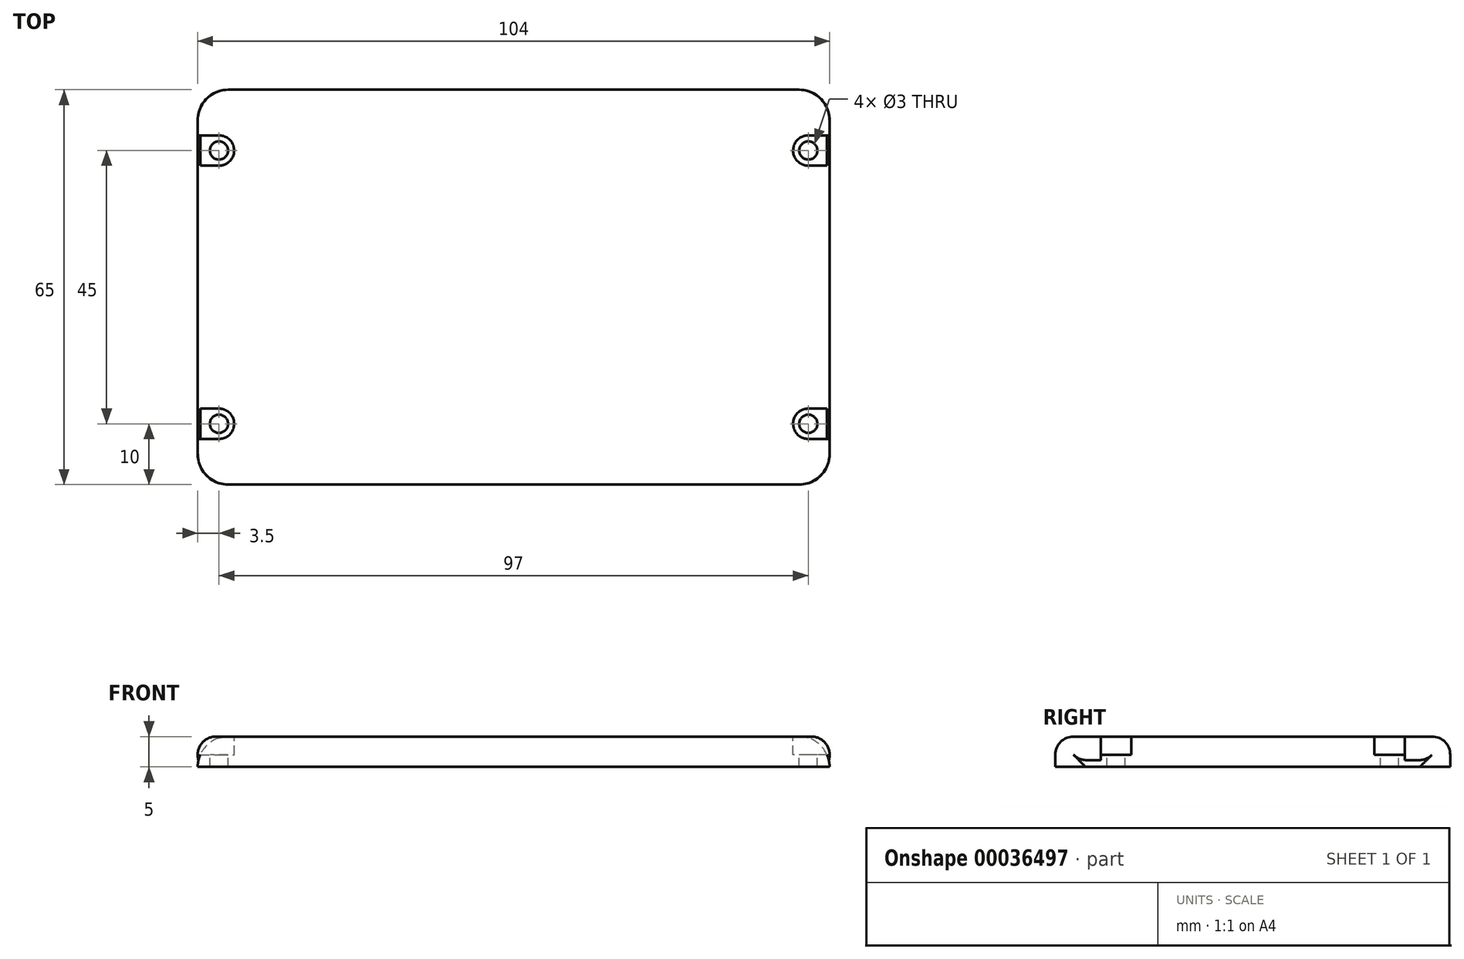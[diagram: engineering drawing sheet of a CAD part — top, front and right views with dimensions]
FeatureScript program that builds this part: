
annotation { "Feature Type Name" : "Feature", "Feature Type Description" : "" }
export const myFeature = defineFeature(function(context is Context, id is Id, definition is map)
    precondition{}
    {
        {
            var Q0;
            Q0=qCreatedBy(makeId("Top.planeOp"),FACE);
            var sketch = newSketch(context, id + "F0", { "sketchPlane" : qUnion([Q0])});
            skLineSegment(sketch, "E0.bottom", {"start": v(5, 0) * mm, "end": v(99, 0) * mm});
            skLineSegment(sketch, "E0.top", {"start": v(5, 65) * mm, "end": v(99, 65) * mm});
            skLineSegment(sketch, "E0.left", {"start": v(0, 5) * mm, "end": v(0, 60) * mm});
            skLineSegment(sketch, "E0.right", {"start": v(104, 5) * mm, "end": v(104, 60) * mm});
            skPoint(sketch, "E1.visualSharp", {"position": v(0, 0) * mm});
            skArc(sketch, "E1.filletArc", {"start": v(0, 5) * mm, "mid": v(1.46, 1.46) * mm, "end": v(5, 0) * mm});
            skPoint(sketch, "E2.visualSharp", {"position": v(0, 65) * mm});
            skArc(sketch, "E2.filletArc", {"start": v(5, 65) * mm, "mid": v(1.46, 63.54) * mm, "end": v(0, 60) * mm});
            skPoint(sketch, "E3.visualSharp", {"position": v(104, 65) * mm});
            skArc(sketch, "E3.filletArc", {"start": v(104, 60) * mm, "mid": v(102.54, 63.54) * mm, "end": v(99, 65) * mm});
            skPoint(sketch, "E4.visualSharp", {"position": v(104, 0) * mm});
            skArc(sketch, "E4.filletArc", {"start": v(99, 0) * mm, "mid": v(102.54, 1.46) * mm, "end": v(104, 5) * mm});
            skSolve(sketch);
        }
        {
            var Q0;
            Q0=makeQuery(id+"F0.imprint","IMPRINT",FACE,{"disambiguationData":[TD([[makeQuery(id+"F0.imprint","IMPRINT",EDGE,{"derivedFrom":sQuery(id+"F0.wireOp",EDGE,"E0.bottom")}),1.0]])]});
            extrude(context, id + "F1", {"entities" : qUnion([Q0]), "depth" : 5 * mm});
        }
        {
            var Q0;
            Q0=makeQuery(id+"F1.opExtrude","CAP_FACE",FACE,{"disambiguationData":[OSD([sQuery(id+"F0.wireOp",EDGE,"E0.bottom"),sQuery(id+"F0.wireOp",EDGE,"E0.top"),sQuery(id+"F0.wireOp",EDGE,"E0.left"),sQuery(id+"F0.wireOp",EDGE,"E0.right"),sQuery(id+"F0.wireOp",EDGE,"E1.filletArc"),sQuery(id+"F0.wireOp",EDGE,"E2.filletArc"),sQuery(id+"F0.wireOp",EDGE,"E3.filletArc"),sQuery(id+"F0.wireOp",EDGE,"E4.filletArc")])],"isStart":false});
            var sketch = newSketch(context, id + "F2", { "sketchPlane" : qUnion([Q0])});
            skCircle(sketch, "E5", {"center": v(3.5, 10) * mm, "radius": 1.5 * mm});
            skCircle(sketch, "E6", {"center": v(100.5, 55) * mm, "radius": 1.5 * mm});
            skLineSegment(sketch, "E7", {"start": v(0, 32.5) * mm, "end": v(104, 32.5) * mm});
            skCircle(sketch, "E8.MirrorC", {"center": v(100.5, 10) * mm, "radius": 1.5 * mm});
            skCircle(sketch, "E9.MirrorC", {"center": v(3.5, 55) * mm, "radius": 1.5 * mm});
            skSolve(sketch);
        }
        {
            var Q0;
            Q0 = qSketchRegion(id + "F2", true);
            extrude(context, id + "F3", {"entities" : qUnion([Q0]), "operationType" : NewBodyOperationType.REMOVE, "oppositeDirection" : true, "depth" : 5 * mm});
        }
        {
            var Q0;
            Q0=makeQuery(id+"F1.opExtrude","CAP_FACE",FACE,{"disambiguationData":[OSD([sQuery(id+"F0.wireOp",EDGE,"E0.bottom"),sQuery(id+"F0.wireOp",EDGE,"E0.top"),sQuery(id+"F0.wireOp",EDGE,"E0.left"),sQuery(id+"F0.wireOp",EDGE,"E0.right"),sQuery(id+"F0.wireOp",EDGE,"E1.filletArc"),sQuery(id+"F0.wireOp",EDGE,"E2.filletArc"),sQuery(id+"F0.wireOp",EDGE,"E3.filletArc"),sQuery(id+"F0.wireOp",EDGE,"E4.filletArc")])],"isStart":false});
            var sketch = newSketch(context, id + "F4", { "sketchPlane" : qUnion([Q0])});
            skLineSegment(sketch, "E10.bottom", {"start": v(0, 12.5) * mm, "end": v(3.5, 12.5) * mm});
            skLineSegment(sketch, "E10.top", {"start": v(0, 7.5) * mm, "end": v(3.5, 7.5) * mm});
            skLineSegment(sketch, "E10.left", {"start": v(0, 12.5) * mm, "end": v(0, 7.5) * mm});
            skLineSegment(sketch, "E10.right", {"start": v(6, 10) * mm, "end": v(6, 10) * mm});
            skPoint(sketch, "E11.visualSharp", {"position": v(6, 12.5) * mm});
            skArc(sketch, "E11.filletArc", {"start": v(6, 10) * mm, "mid": v(5.27, 11.77) * mm, "end": v(3.5, 12.5) * mm});
            skPoint(sketch, "E12.visualSharp", {"position": v(6, 7.5) * mm});
            skArc(sketch, "E12.filletArc", {"start": v(3.5, 7.5) * mm, "mid": v(5.27, 8.23) * mm, "end": v(6, 10) * mm});
            skLineSegment(sketch, "E13.bottom", {"start": v(104, 52.5) * mm, "end": v(100.5, 52.5) * mm});
            skLineSegment(sketch, "E13.top", {"start": v(104, 57.5) * mm, "end": v(100.5, 57.5) * mm});
            skLineSegment(sketch, "E13.left", {"start": v(104, 52.5) * mm, "end": v(104, 57.5) * mm});
            skLineSegment(sketch, "E13.right", {"start": v(98, 55) * mm, "end": v(98, 55) * mm});
            skPoint(sketch, "E14.visualSharp", {"position": v(98, 52.5) * mm});
            skArc(sketch, "E14.filletArc", {"start": v(98, 55) * mm, "mid": v(98.73, 53.23) * mm, "end": v(100.5, 52.5) * mm});
            skPoint(sketch, "E15.visualSharp", {"position": v(98, 57.5) * mm});
            skArc(sketch, "E15.filletArc", {"start": v(100.5, 57.5) * mm, "mid": v(98.73, 56.77) * mm, "end": v(98, 55) * mm});
            skLineSegment(sketch, "E16", {"start": v(0, 32.5) * mm, "end": v(104, 32.5) * mm});
            skLineSegment(sketch, "E17.MirrorCS", {"start": v(0, 52.5) * mm, "end": v(0, 57.5) * mm});
            skLineSegment(sketch, "E18.MirrorCS", {"start": v(0, 52.5) * mm, "end": v(3.5, 52.5) * mm});
            skArc(sketch, "E19.MirrorCS", {"start": v(6, 55) * mm, "mid": v(5.27, 53.23) * mm, "end": v(3.5, 52.5) * mm});
            skArc(sketch, "E20.MirrorCS", {"start": v(3.5, 57.5) * mm, "mid": v(5.27, 56.77) * mm, "end": v(6, 55) * mm});
            skLineSegment(sketch, "E21.MirrorCS", {"start": v(0, 57.5) * mm, "end": v(3.5, 57.5) * mm});
            skLineSegment(sketch, "E22.MirrorCS", {"start": v(104, 12.5) * mm, "end": v(100.5, 12.5) * mm});
            skArc(sketch, "E23.MirrorCS", {"start": v(98, 10) * mm, "mid": v(98.73, 11.77) * mm, "end": v(100.5, 12.5) * mm});
            skArc(sketch, "E24.MirrorCS", {"start": v(100.5, 7.5) * mm, "mid": v(98.73, 8.23) * mm, "end": v(98, 10) * mm});
            skLineSegment(sketch, "E25.MirrorCS", {"start": v(104, 7.5) * mm, "end": v(100.5, 7.5) * mm});
            skLineSegment(sketch, "E26.MirrorCS", {"start": v(104, 12.5) * mm, "end": v(104, 7.5) * mm});
            skSolve(sketch);
        }
        {
            var Q0;
            Q0 = qSketchRegion(id + "F4", true);
            extrude(context, id + "F5", {"entities" : qUnion([Q0]), "operationType" : NewBodyOperationType.REMOVE, "oppositeDirection" : true, "depth" : 3 * mm});
        }
        {
            var Q0;
            {var subQ0=sQuery(id+"F0.wireOp",EDGE,"E0.right");var subQ1=sQuery(id+"F0.wireOp",EDGE,"E4.filletArc");Q0=makeQuery(id+"F5.boolean.opBoolean","SPLIT",EDGE,{"disambiguationData":[TD([makeQuery(id+"F1.opExtrude","SWEPT_FACE",FACE,{"disambiguationData":[OSD([subQ1])]})])],"derivedFrom":makeQuery(id+"F1.opExtrude","CAP_EDGE",EDGE,{"disambiguationData":[OSD([subQ0])],"isStart":false})});}
            fillet(context, id + "F6", {"entities" : qUnion([Q0]), "radius" : 3 * mm, "tangentPropagation" : true, "allowEdgeOverflow" : false});
        }
        {
            var Q0;
            Q0=makeQuery(id+"F1.opExtrude","CAP_EDGE",EDGE,{"disambiguationData":[OSD([sQuery(id+"F0.wireOp",EDGE,"E0.top")])],"isStart":false});
            fillet(context, id + "F7", {"entities" : qUnion([Q0]), "radius" : 3 * mm, "tangentPropagation" : true, "allowEdgeOverflow" : false});
        }
        {
            var Q0;
            {var subQ0=sQuery(id+"F0.wireOp",EDGE,"E0.left");Q0=makeQuery(id+"F5.boolean.opBoolean","SPLIT",EDGE,{"disambiguationData":[TD([makeQuery(id+"F5.opExtrude","SWEPT_FACE",FACE,{"disambiguationData":[OSD([sQuery(id+"F4.wireOp",EDGE,"E10.bottom")])]})])],"derivedFrom":makeQuery(id+"F1.opExtrude","CAP_EDGE",EDGE,{"disambiguationData":[OSD([subQ0])],"isStart":false})});}
            var Q1;
            {var subQ0=sQuery(id+"F0.wireOp",EDGE,"E0.right");Q1=makeQuery(id+"F5.boolean.opBoolean","SPLIT",EDGE,{"disambiguationData":[TD([makeQuery(id+"F5.opExtrude","SWEPT_FACE",FACE,{"disambiguationData":[OSD([sQuery(id+"F4.wireOp",EDGE,"E13.bottom")])]})])],"derivedFrom":makeQuery(id+"F1.opExtrude","CAP_EDGE",EDGE,{"disambiguationData":[OSD([subQ0])],"isStart":false})});}
            fillet(context, id + "F8", {"entities" : qUnion([Q0, Q1]), "radius" : 5 * mm, "tangentPropagation" : true, "allowEdgeOverflow" : false});
        }
    });
